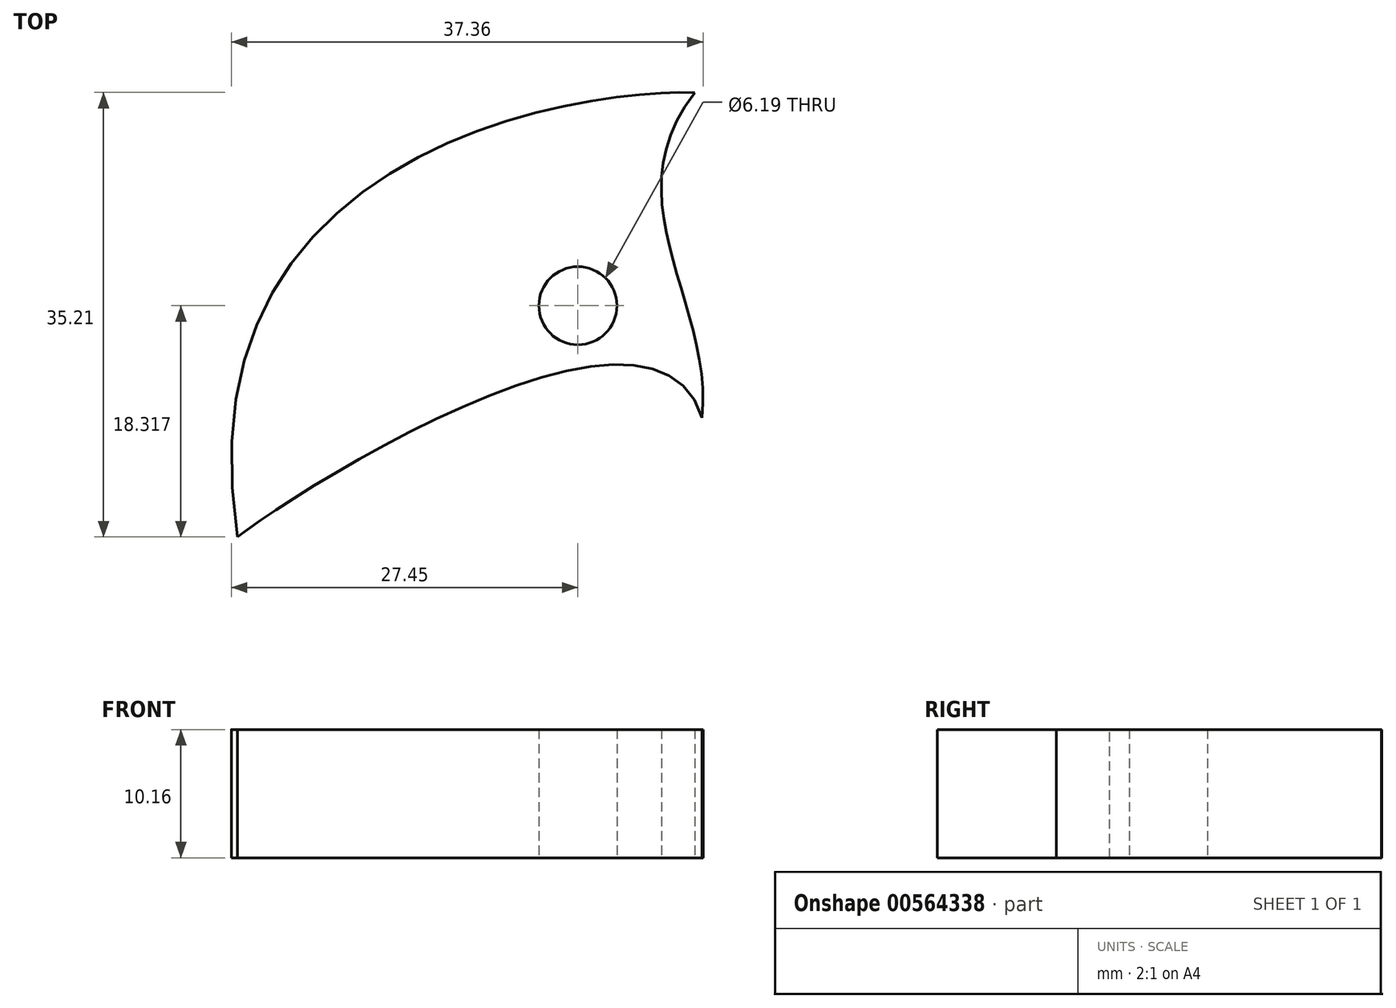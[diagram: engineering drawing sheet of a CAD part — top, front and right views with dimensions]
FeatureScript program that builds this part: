
annotation { "Feature Type Name" : "Feature", "Feature Type Description" : "" }
export const myFeature = defineFeature(function(context is Context, id is Id, definition is map)
    precondition{}
    {
        {
            var Q0;
            Q0=qCreatedBy(makeId("Top.planeOp"),FACE);
            var sketch = newSketch(context, id + "F0", { "sketchPlane" : qUnion([Q0])});
            skFitSpline(sketch, "E0", {"points": [v(9.84, -3.23) * mm, v(-26.96, -12.67) * mm], "startDerivative": vector(-11.23, 36.63) * mm, "endDerivative": vector(-15.14, -11.72) * mm});
            skFitSpline(sketch, "E1", {"points": [v(9.25, 22.53) * mm, v(-26.96, -12.67) * mm], "startDerivative": vector(-24.9, 0.98) * mm, "endDerivative": vector(14.65, -93.78) * mm});
            skFitSpline(sketch, "E2", {"points": [v(9.84, -3.23) * mm, v(9.25, 22.53) * mm], "startDerivative": vector(2.77, 27.19) * mm, "endDerivative": vector(20.03, 25.89) * mm});
            skCircle(sketch, "E3", {"center": v(0, 5.65) * mm, "radius": 3.1 * mm});
            skSolve(sketch);
        }
        {
            var Q0;
            Q0=makeQuery(id+"F0.imprint","IMPRINT",FACE,{"disambiguationData":[TD([[makeQuery(id+"F0.imprint","IMPRINT",EDGE,{"derivedFrom":sQuery(id+"F0.wireOp",EDGE,"E0")}),-1.0]])]});
            extrude(context, id + "F1", {"entities" : qUnion([Q0]), "depth" : 10.16 * mm, "offsetDistance" : 25.4 * mm});
        }
    });
